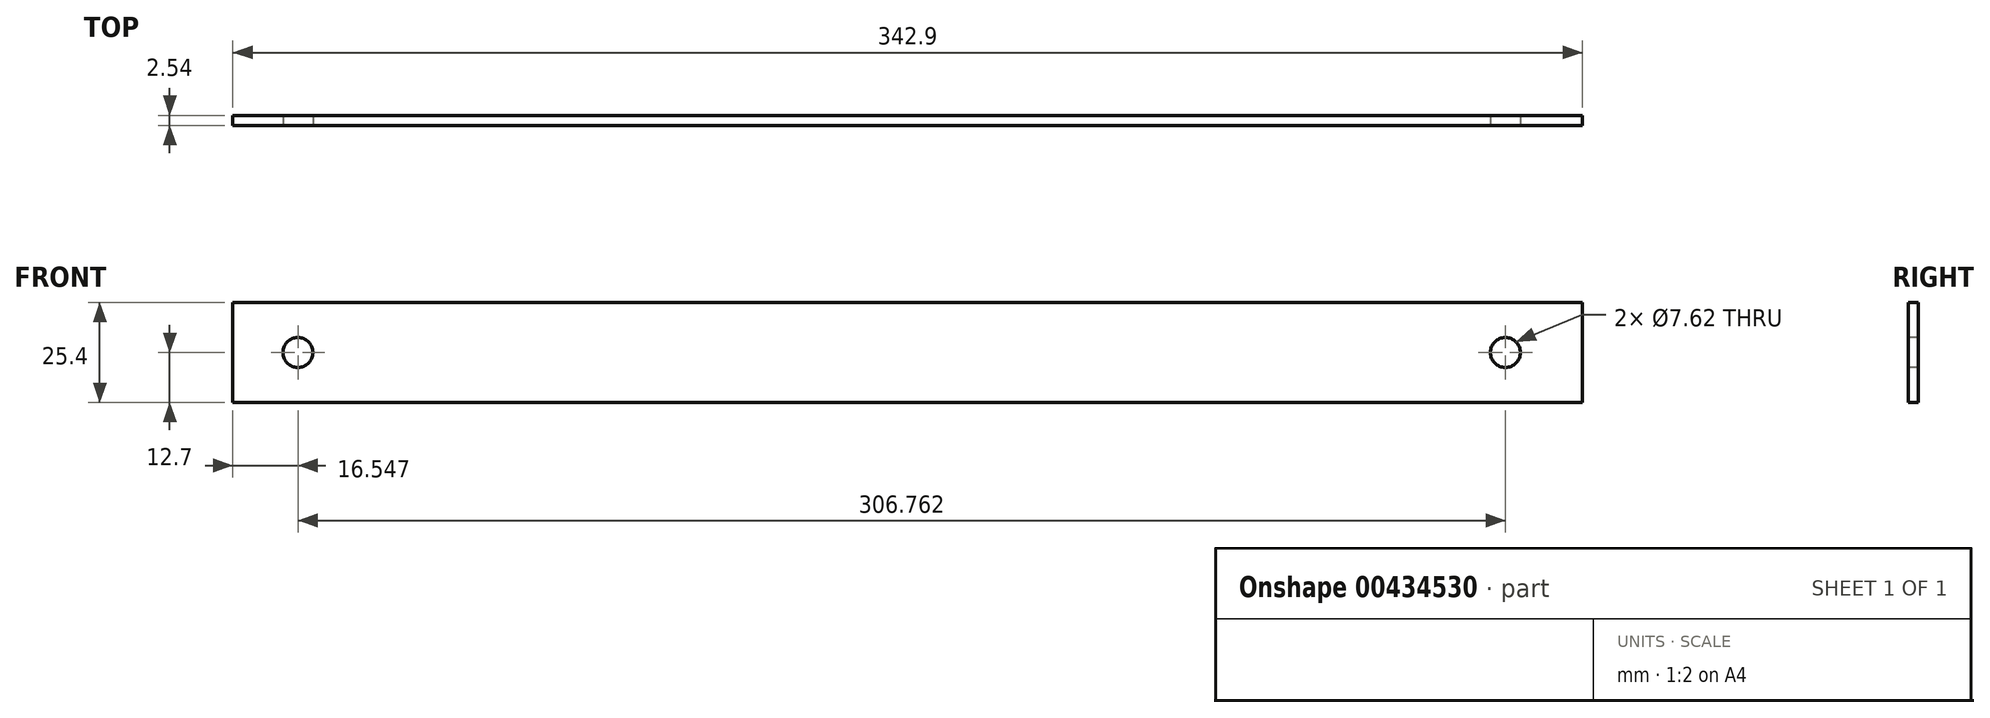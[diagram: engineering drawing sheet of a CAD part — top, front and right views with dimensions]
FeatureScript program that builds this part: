
annotation { "Feature Type Name" : "Feature", "Feature Type Description" : "" }
export const myFeature = defineFeature(function(context is Context, id is Id, definition is map)
    precondition{}
    {
        {
            var Q0;
            Q0=qCreatedBy(makeId("Front.planeOp"),FACE);
            var sketch = newSketch(context, id + "F0", { "sketchPlane" : qUnion([Q0])});
            skLineSegment(sketch, "E0.bottom", {"start": v(-171.45, 12.7) * mm, "end": v(171.45, 12.7) * mm});
            skLineSegment(sketch, "E0.top", {"start": v(-171.45, -12.7) * mm, "end": v(171.45, -12.7) * mm});
            skLineSegment(sketch, "E0.left", {"start": v(-171.45, 12.7) * mm, "end": v(-171.45, -12.7) * mm});
            skLineSegment(sketch, "E0.right", {"start": v(171.45, 12.7) * mm, "end": v(171.45, -12.7) * mm});
            skPoint(sketch, "E0.middle", {"position": v(0, 0) * mm});
            skSolve(sketch);
        }
        {
            var Q0;
            Q0=makeQuery(id+"F0.imprint","IMPRINT",FACE,{"disambiguationData":[TD([[makeQuery(id+"F0.imprint","IMPRINT",EDGE,{"derivedFrom":sQuery(id+"F0.wireOp",EDGE,"E0.bottom")}),-1.0]])]});
            extrude(context, id + "F1", {"entities" : qUnion([Q0]), "endBound" : BoundingType.SYMMETRIC, "depth" : 2.54 * mm});
        }
        {
            var Q0;
            Q0=makeQuery(id+"F1.opExtrude","CAP_FACE",FACE,{"disambiguationData":[OSD([sQuery(id+"F0.wireOp",EDGE,"E0.bottom"),sQuery(id+"F0.wireOp",EDGE,"E0.top"),sQuery(id+"F0.wireOp",EDGE,"E0.left"),sQuery(id+"F0.wireOp",EDGE,"E0.right")])],"isStart":false});
            var sketch = newSketch(context, id + "F2", { "sketchPlane" : qUnion([Q0])});
            skCircle(sketch, "E1", {"center": v(151.86, 0) * mm, "radius": 4.77 * mm});
            skCircle(sketch, "E2", {"center": v(-154.9, 0) * mm, "radius": 3.81 * mm});
            skPoint(sketch, "E3", {"position": v(-171.45, 0) * mm});
            skSolve(sketch);
        }
        {
            var Q0;
            Q0=sQuery(id+"F2.wireOp",VERTEX,"E1.center");
            var Q1;
            Q1=sQuery(id+"F2.wireOp",VERTEX,"E2.center");
            var Q2;
            Q2=makeQuery(id+"F1.opExtrude","SWEPT_BODY",BODY,{"disambiguationData":[OSD([sQuery(id+"F0.wireOp",EDGE,"E0.bottom"),sQuery(id+"F0.wireOp",EDGE,"E0.top"),sQuery(id+"F0.wireOp",EDGE,"E0.left"),sQuery(id+"F0.wireOp",EDGE,"E0.right")])]});
            hole(context, id + "F3", {"style" : HoleStyle.SIMPLE, "endStyle" : HoleEndStyle.THROUGH, "holeDiameter" : 7.62 * mm, "isTappedThrough" : true, "tappedDepth" : 12.7 * mm, "tapClearance" : 3, "locations" : qUnion([Q0, Q1]), "scope" : qUnion([Q2])});
        }
    });
